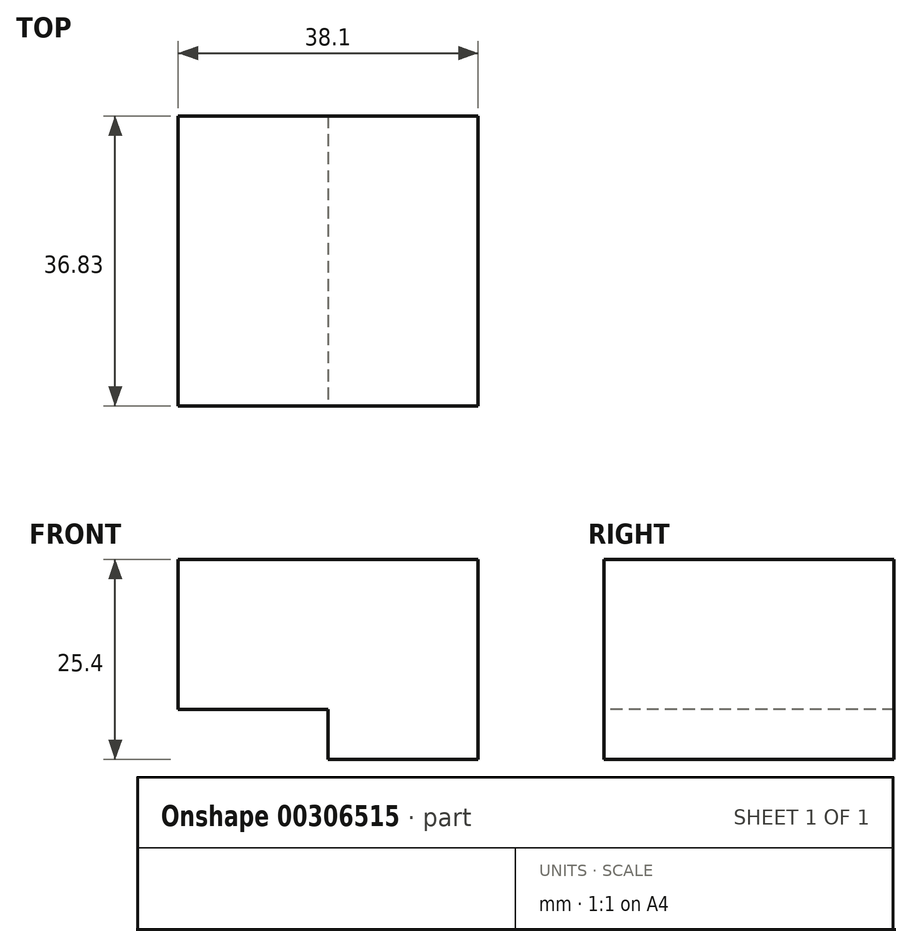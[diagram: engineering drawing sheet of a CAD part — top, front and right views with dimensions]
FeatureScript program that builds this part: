
annotation { "Feature Type Name" : "Feature", "Feature Type Description" : "" }
export const myFeature = defineFeature(function(context is Context, id is Id, definition is map)
    precondition{}
    {
        {
            var Q0;
            Q0=qCreatedBy(makeId("Front.planeOp"),FACE);
            var sketch = newSketch(context, id + "F0", { "sketchPlane" : qUnion([Q0])});
            skLineSegment(sketch, "E0", {"start": v(-18.4, 0) * mm, "end": v(-18.4, 19.05) * mm});
            skLineSegment(sketch, "E1", {"start": v(-18.4, 19.05) * mm, "end": v(-37.45, 19.05) * mm});
            skLineSegment(sketch, "E2", {"start": v(-37.45, 19.05) * mm, "end": v(-37.45, 0) * mm});
            skLineSegment(sketch, "E3", {"start": v(-37.45, 0) * mm, "end": v(-18.4, 0) * mm});
            skLineSegment(sketch, "E4", {"start": v(-18.4, 19.05) * mm, "end": v(-18.4, 25.4) * mm});
            skLineSegment(sketch, "E5", {"start": v(-18.4, 25.4) * mm, "end": v(-37.45, 25.4) * mm});
            skLineSegment(sketch, "E6", {"start": v(-37.45, 25.4) * mm, "end": v(-37.45, 19.05) * mm});
            skLineSegment(sketch, "E7", {"start": v(-37.45, 25.4) * mm, "end": v(-56.5, 25.4) * mm});
            skLineSegment(sketch, "E8", {"start": v(-56.5, 25.4) * mm, "end": v(-56.5, 6.35) * mm});
            skLineSegment(sketch, "E9", {"start": v(-56.5, 6.35) * mm, "end": v(-37.45, 6.35) * mm});
            skSolve(sketch);
        }
        {
            var Q0;
            {var subQ0=sQuery(id+"F0.wireOp",EDGE,"E6");Q0=makeQuery(id+"F0.imprint","IMPRINT",FACE,{"disambiguationData":[TD([[makeQuery(id+"F0.imprint","IMPRINT",EDGE,{"derivedFrom":subQ0}),-1.0]])]});}
            var Q1;
            Q1=makeQuery(id+"F0.imprint","IMPRINT",FACE,{"disambiguationData":[TD([[makeQuery(id+"F0.imprint","IMPRINT",EDGE,{"derivedFrom":sQuery(id+"F0.wireOp",EDGE,"E1")}),-1.0]])]});
            var Q2;
            Q2=makeQuery(id+"F0.imprint","IMPRINT",FACE,{"disambiguationData":[TD([[makeQuery(id+"F0.imprint","IMPRINT",EDGE,{"derivedFrom":sQuery(id+"F0.wireOp",EDGE,"E0")}),1.0]])]});
            extrude(context, id + "F1", {"entities" : qUnion([Q0, Q1, Q2]), "oppositeDirection" : true, "depth" : 36.83 * mm});
        }
    });
